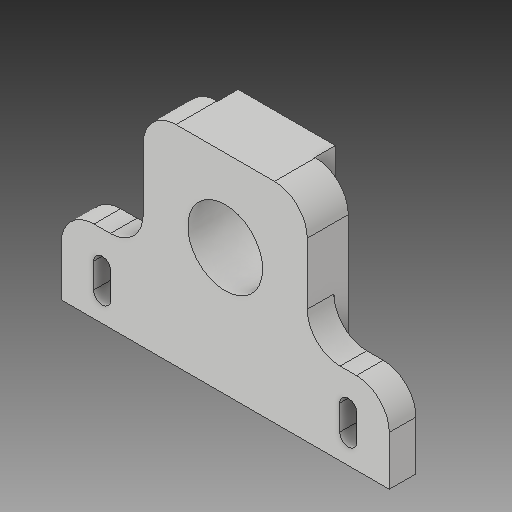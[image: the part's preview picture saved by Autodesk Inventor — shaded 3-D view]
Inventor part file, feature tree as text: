
AUTODESK INVENTOR PART (.ipt)
format: ipt  version: 2018 (Build 220112000, 112)  size: 175,616 bytes
history: native  units: in
note: dims shown in document units (in); Inventor stores cm internally (conversion verified against a paired STEP export)
features: extrude x5, sketch x5, fillet x1, mirror x1
ambient origin geometry x8: Origin, YZ Plane, XZ Plane, XY Plane, X Axis, Y Axis, Z Axis, Center Point
bodies: Solid1 (feature_tree)
feature tree (12):
  extrude  "Extrusion1"  Depth=0.7874in
  sketch  "Sketch2"  dims[d2=1.5748in d3=1.2205in]
  extrude  "Extrusion2"  Depth=1.2205in
  extrude  "Extrusion3"  Depth=0.2559in
  extrude  "Extrusion4"  Depth=0.7874in
  fillet  "Fillet1"  Radius=0.7185in
  extrude  "Extrusion5"  Depth=0.9331in
  mirror  "Mirror1"
  sketch  "Sketch1"  dims[d0=3.1496in d1=0.7874in]
  sketch  "Sketch3"  dims[d4=0.2559in d5=0.0in d6=0.7185in]
  sketch  "Sketch4"  dims[d7=0.7874in d8=0.7874in d9=0.7185in]
  sketch  "Sketch5"  dims[d10=0.1378in d11=0.0in d12=0.9331in d13=0.1969in d14=0.0in d15=0.1969in d16=0.0in d17=0.315in d18=0.1654in d19=0.2409in d20=0.3937in d21=0.2362in d22=0.1969in d23=0.0in]
